# Revit family: ToothbrushHolder-Vitra-OriginSeries-A44889
name_source: partatom
category: Plumbing Fixtures
revit_build: Autodesk Revit 2017 (Build: 20160225_1515(x64)
units: mm (PartAtom-declared; Revit-internal decimal feet)

## family parameters
Cut with Voids When Loaded = No
Host = Face
OmniClass Number = 23.45.00.00
OmniClass Title = Sanitary, Laundry, and Cleaning Equipment
Part Type = Normal
Room Calculation Point = No
Round Connector Dimension = Use Diameter
Shared = Yes

## types (4) — shared parameters
BIMobject category = Sanitary - Accessories
Brand = VitrA
CW Connection = No
Description = Origin Toothbrush Holder
Design country = Turkey
HW Connection = No
IFC Classification = Sanitary Terminal
Main Material = Metal
Manufacturer = Vitra
Manufacturer name = Vitra
Masterformat 2014 Code = 10 28 16
Masterformat 2014 Description = Bath Accessories
Mounting type = Countertop
NBS Referans Code = 35-75-89
NBS Referans Description = Toothbrush Holders
Nominal Depth (mm) = 70 mm  [stored 0.229659 ft]
Nominal Height (mm) = 105 mm  [stored 0.344488 ft]
Nominal Width (mm) = 70 mm  [stored 0.229659 ft]
OmniClass Code = 23-31 25 00
OmniClass Description = Toilet and Bath Specialties
Product Type = Countertop Toothbrush Holder
Product certification = https://www.vitraglobal.com
Product family = OriginSeries
Product group = Toothbrush Holder
Product url = https://www.vitraglobal.com
Technical description = https://www.vitraglobal.com
UNSPSC Description = Furniture and Furnishings
URL = https://vitraglobal.com
Uniclass 1.4 Code = L824
Uniclass 1.4 Description = Bathroom, toilet furniture and fittings
Uniclass 2.0 Code = PR-35-75-89
Uniclass 2.0 Description = Toothbrush Holders
Uniclass 2015 Code = Pr_40_20_76_89
Uniclass 2015 Name = Toothbrush holders
Uniformat II Code = E1090
Uniformat II Description = Other Equipment
Vent Connection = No
Warranty Period (Year) = 5 Years
Waste Connection = No
Youtube = https://www.youtube.com
zero-valued in all types: Default Elevation

## per-type parameters (varying)
| type | Article No. (default) | Coating Material | Color | Model | Product SKU | Product data url |
| ToothBrushHolder-Vitra-OriginSeries-A44889 | A44889 | Chrome | Chrome | A44889 | A44889 | https://www.bimobject.com |
| ToothBrushHolder-Vitra-OriginSeries-A4488934 | A4488934 | Brushed Nickel | Brushed Nickel | A4488934 | A4488934 | https://www.vitraglobal.com |
| ToothBrushHolder-Vitra-OriginSeries-A4488936 | A4488936 | Black | Black | A4488936 | A4488936 | https://www.vitraglobal.com |
| ToothBrushHolder-Vitra-OriginSeries-A4488926 | A4488926 | BrightCopper | Copper | A4488926 | A4488926 | https://www.vitraglobal.com |

note: [stored X ft] marks values corroborated as IEEE doubles in the binary element streams (Revit-internal decimal feet)

## geometry (parser evidence)
native form markers: Sweep x2
no freeform markers — native parametric forms only
